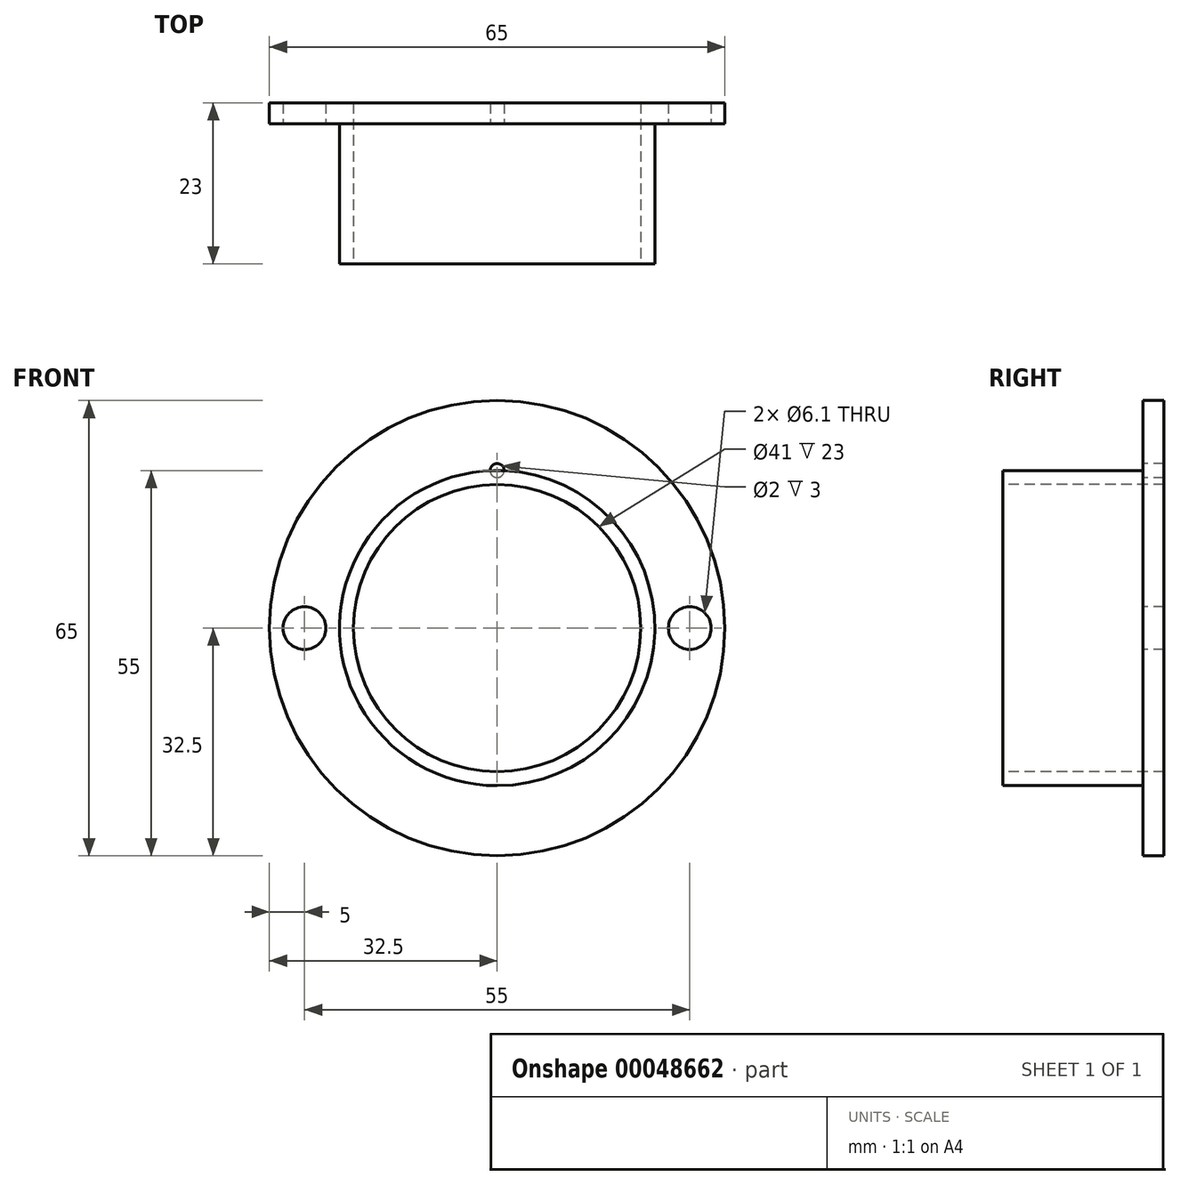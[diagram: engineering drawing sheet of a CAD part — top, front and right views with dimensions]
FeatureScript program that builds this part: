
annotation { "Feature Type Name" : "Feature", "Feature Type Description" : "" }
export const myFeature = defineFeature(function(context is Context, id is Id, definition is map)
    precondition{}
    {
        {
            var Q0;
            Q0=qCreatedBy(makeId("Front.planeOp"),FACE);
            var sketch = newSketch(context, id + "F0", { "sketchPlane" : qUnion([Q0])});
            skCircle(sketch, "E0", {"center": v(0, 0) * mm, "radius": 32.5 * mm});
            skSolve(sketch);
        }
        {
            var Q0;
            Q0 = qSketchRegion(id + "F0", true);
            extrude(context, id + "F1", {"entities" : qUnion([Q0]), "depth" : 3 * mm});
        }
        {
            var Q0;
            Q0=makeQuery(id+"F1.opExtrude","CAP_FACE",FACE,{"disambiguationData":[OSD([sQuery(id+"F0.wireOp",EDGE,"E0")])],"isStart":false});
            var sketch = newSketch(context, id + "F2", { "sketchPlane" : qUnion([Q0])});
            skCircle(sketch, "E1", {"center": v(0, 0) * mm, "radius": 22.5 * mm});
            skSolve(sketch);
        }
        {
            var Q0;
            Q0 = qSketchRegion(id + "F2", true);
            extrude(context, id + "F3", {"entities" : qUnion([Q0]), "operationType" : NewBodyOperationType.ADD, "depth" : 20 * mm});
        }
        {
            var Q0;
            Q0=makeQuery(id+"F3.opExtrude","CAP_FACE",FACE,{"disambiguationData":[OSD([sQuery(id+"F2.wireOp",EDGE,"E1")])],"isStart":false});
            var sketch = newSketch(context, id + "F4", { "sketchPlane" : qUnion([Q0])});
            skCircle(sketch, "E2", {"center": v(0, 0) * mm, "radius": 20.5 * mm});
            skSolve(sketch);
        }
        {
            var Q0;
            Q0 = qSketchRegion(id + "F4", true);
            extrude(context, id + "F5", {"entities" : qUnion([Q0]), "operationType" : NewBodyOperationType.REMOVE, "endBound" : BoundingType.THROUGH_ALL, "oppositeDirection" : true, "depth" : 25 * mm});
        }
        {
            var Q0;
            Q0=makeQuery(id+"F1.opExtrude","CAP_FACE",FACE,{"disambiguationData":[OSD([sQuery(id+"F0.wireOp",EDGE,"E0")])],"isStart":false});
            var sketch = newSketch(context, id + "F6", { "sketchPlane" : qUnion([Q0])});
            skCircle(sketch, "E3", {"center": v(27.5, 0) * mm, "radius": 3.05 * mm});
            skCircle(sketch, "E4", {"center": v(-27.5, 0) * mm, "radius": 3.05 * mm});
            skCircle(sketch, "E5", {"center": v(0, 22.5) * mm, "radius": 1 * mm});
            skSolve(sketch);
        }
        {
            var Q0;
            Q0 = qSketchRegion(id + "F6", true);
            extrude(context, id + "F7", {"entities" : qUnion([Q0]), "operationType" : NewBodyOperationType.REMOVE, "endBound" : BoundingType.THROUGH_ALL, "oppositeDirection" : true, "depth" : 25 * mm});
        }
    });
